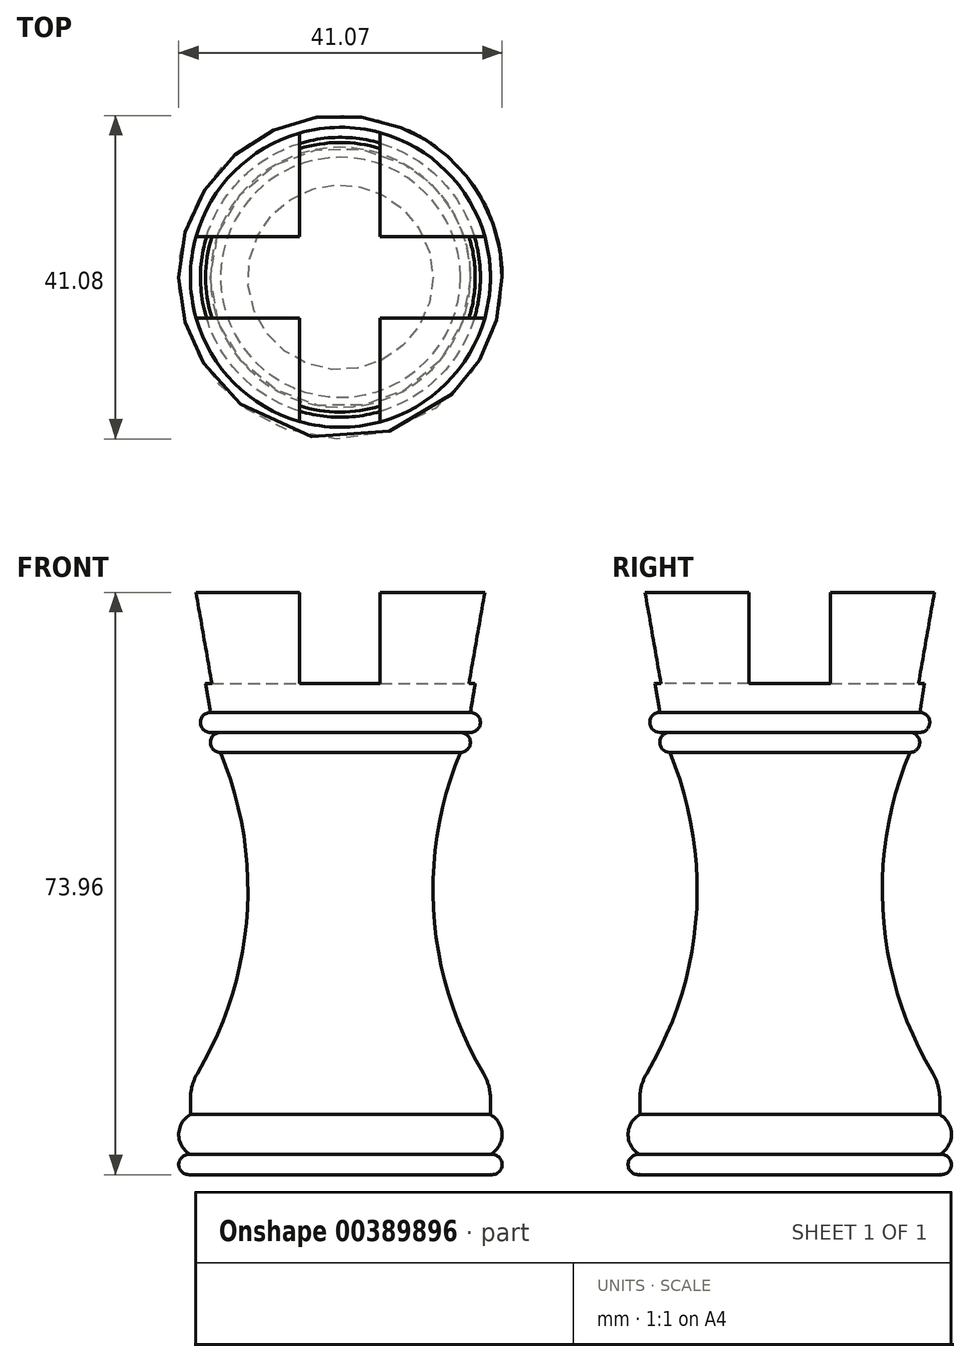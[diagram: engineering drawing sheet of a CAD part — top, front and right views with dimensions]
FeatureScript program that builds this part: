
annotation { "Feature Type Name" : "Feature", "Feature Type Description" : "" }
export const myFeature = defineFeature(function(context is Context, id is Id, definition is map)
    precondition{}
    {
        {
            var Q0;
            Q0=qCreatedBy(makeId("Front.planeOp"),FACE);
            var sketch = newSketch(context, id + "F0", { "sketchPlane" : qUnion([Q0])});
            skLineSegment(sketch, "E0", {"start": v(-58.9, -34.46) * mm, "end": v(-39.86, -34.46) * mm});
            skLineSegment(sketch, "E1", {"start": v(-58.9, -29.38) * mm, "end": v(-39.86, -29.38) * mm});
            skLineSegment(sketch, "E2", {"start": v(-39.86, -34.46) * mm, "end": v(-39.86, -29.38) * mm});
            skLineSegment(sketch, "E3", {"start": v(-58.9, -37) * mm, "end": v(-39.86, -37) * mm});
            skArc(sketch, "E4", {"start": v(-58.9, -34.46) * mm, "mid": v(-60.4, -35.73) * mm, "end": v(-58.9, -37) * mm});
            skArc(sketch, "E5", {"start": v(-58.9, -29.38) * mm, "mid": v(-60.4, -31.92) * mm, "end": v(-58.9, -34.46) * mm});
            skLineSegment(sketch, "E6", {"start": v(-56.37, 21.7) * mm, "end": v(-58.9, 36.94) * mm});
            skLineSegment(sketch, "E7", {"start": v(-39.86, 36.94) * mm, "end": v(-39.86, -37) * mm});
            skLineSegment(sketch, "E8", {"start": v(-58.9, 36.94) * mm, "end": v(-49.38, 36.94) * mm});
            skLineSegment(sketch, "E9", {"start": v(-39.86, 36.94) * mm, "end": v(-49.38, 36.94) * mm});
            skLineSegment(sketch, "E10", {"start": v(-56.37, 21.7) * mm, "end": v(-39.86, 21.7) * mm});
            skLineSegment(sketch, "E11", {"start": v(-56.37, 21.7) * mm, "end": v(-56.37, 19.16) * mm});
            skLineSegment(sketch, "E12", {"start": v(-56.37, 19.16) * mm, "end": v(-55.1, 19.16) * mm});
            skLineSegment(sketch, "E13", {"start": v(-55.1, 19.16) * mm, "end": v(-39.86, 19.16) * mm});
            skLineSegment(sketch, "E14", {"start": v(-55.1, 16.62) * mm, "end": v(-39.86, 16.62) * mm});
            skPoint(sketch, "E15", {"position": v(-56.37, 17.89) * mm});
            skArc(sketch, "E16", {"start": v(-55.1, 19.16) * mm, "mid": v(-56.37, 17.89) * mm, "end": v(-55.1, 16.62) * mm});
            skLineSegment(sketch, "E17", {"start": v(-56.37, 20.43) * mm, "end": v(-57.64, 20.43) * mm});
            skArc(sketch, "E18", {"start": v(-56.37, 21.7) * mm, "mid": v(-57.64, 20.43) * mm, "end": v(-56.37, 19.16) * mm});
            skLineSegment(sketch, "E19", {"start": v(-58.9, -29.38) * mm, "end": v(-58.9, -27.38) * mm});
            skArc(sketch, "E20", {"start": v(-58.01, -24.13) * mm, "mid": v(-51.73, -4.1) * mm, "end": v(-55.1, 16.62) * mm});
            skArc(sketch, "E21.filletArc", {"start": v(-58.01, -24.13) * mm, "mid": v(-58.68, -25.7) * mm, "end": v(-58.9, -27.38) * mm});
            skSolve(sketch);
        }
        {
            var Q0;
            Q0=qSketchRegion(id+"F0",true);
            var Q1;
            Q1=sQuery(id+"F0.wireOp",EDGE,"E7");
            revolve(context, id + "F1", {"entities" : qUnion([Q0]), "axis" : qUnion([Q1]), "revolveType" : RevolveType.FULL});
        }
        {
            var Q0;
            Q0=qCreatedBy(makeId("Top.planeOp"),FACE);
            var sketch = newSketch(context, id + "F2", { "sketchPlane" : qUnion([Q0])});
            skLineSegment(sketch, "E22", {"start": v(-34.8, -5.16) * mm, "end": v(-19.38, -5.16) * mm});
            skLineSegment(sketch, "E23", {"start": v(-19.38, -5.16) * mm, "end": v(-19.38, 5.16) * mm});
            skLineSegment(sketch, "E24", {"start": v(-29.66, 5.16) * mm, "end": v(-19.38, 5.16) * mm});
            skLineSegment(sketch, "E25", {"start": v(-29.66, 5.16) * mm, "end": v(-34.8, 5.16) * mm});
            skLineSegment(sketch, "E26", {"start": v(-34.8, 5.16) * mm, "end": v(-34.8, 20.63) * mm});
            skLineSegment(sketch, "E27", {"start": v(-34.8, 20.63) * mm, "end": v(-39.94, 20.63) * mm});
            skLineSegment(sketch, "E28.MirrorCS", {"start": v(-45.08, 5.16) * mm, "end": v(-45.08, 20.63) * mm});
            skLineSegment(sketch, "E29.MirrorCS", {"start": v(-50.22, 5.16) * mm, "end": v(-45.08, 5.16) * mm});
            skLineSegment(sketch, "E30.MirrorCS", {"start": v(-50.22, 5.16) * mm, "end": v(-60.5, 5.16) * mm});
            skLineSegment(sketch, "E31.MirrorCS", {"start": v(-60.5, -5.16) * mm, "end": v(-60.5, 5.16) * mm});
            skLineSegment(sketch, "E32.MirrorCS", {"start": v(-45.08, -5.16) * mm, "end": v(-60.5, -5.16) * mm});
            skLineSegment(sketch, "E33.MirrorCS", {"start": v(-45.08, 20.63) * mm, "end": v(-39.94, 20.63) * mm});
            skLineSegment(sketch, "E34.MirrorCS", {"start": v(-45.08, -5.16) * mm, "end": v(-45.08, -20.63) * mm});
            skLineSegment(sketch, "E35.MirrorCS", {"start": v(-34.8, -5.16) * mm, "end": v(-34.8, -20.63) * mm});
            skLineSegment(sketch, "E36.MirrorCS", {"start": v(-34.8, -20.63) * mm, "end": v(-39.94, -20.63) * mm});
            skLineSegment(sketch, "E37.MirrorCS", {"start": v(-45.08, -20.63) * mm, "end": v(-39.94, -20.63) * mm});
            skSolve(sketch);
        }
        {
            var Q0;
            Q0=qSketchRegion(id+"F2",true);
            extrude(context, id + "F3", {"entities" : qUnion([Q0]), "operationType" : NewBodyOperationType.REMOVE, "depth" : 50.8 * mm, "hasSecondDirection" : true, "secondDirectionOppositeDirection" : false, "secondDirectionDepth" : 25.4 * mm});
        }
    });
